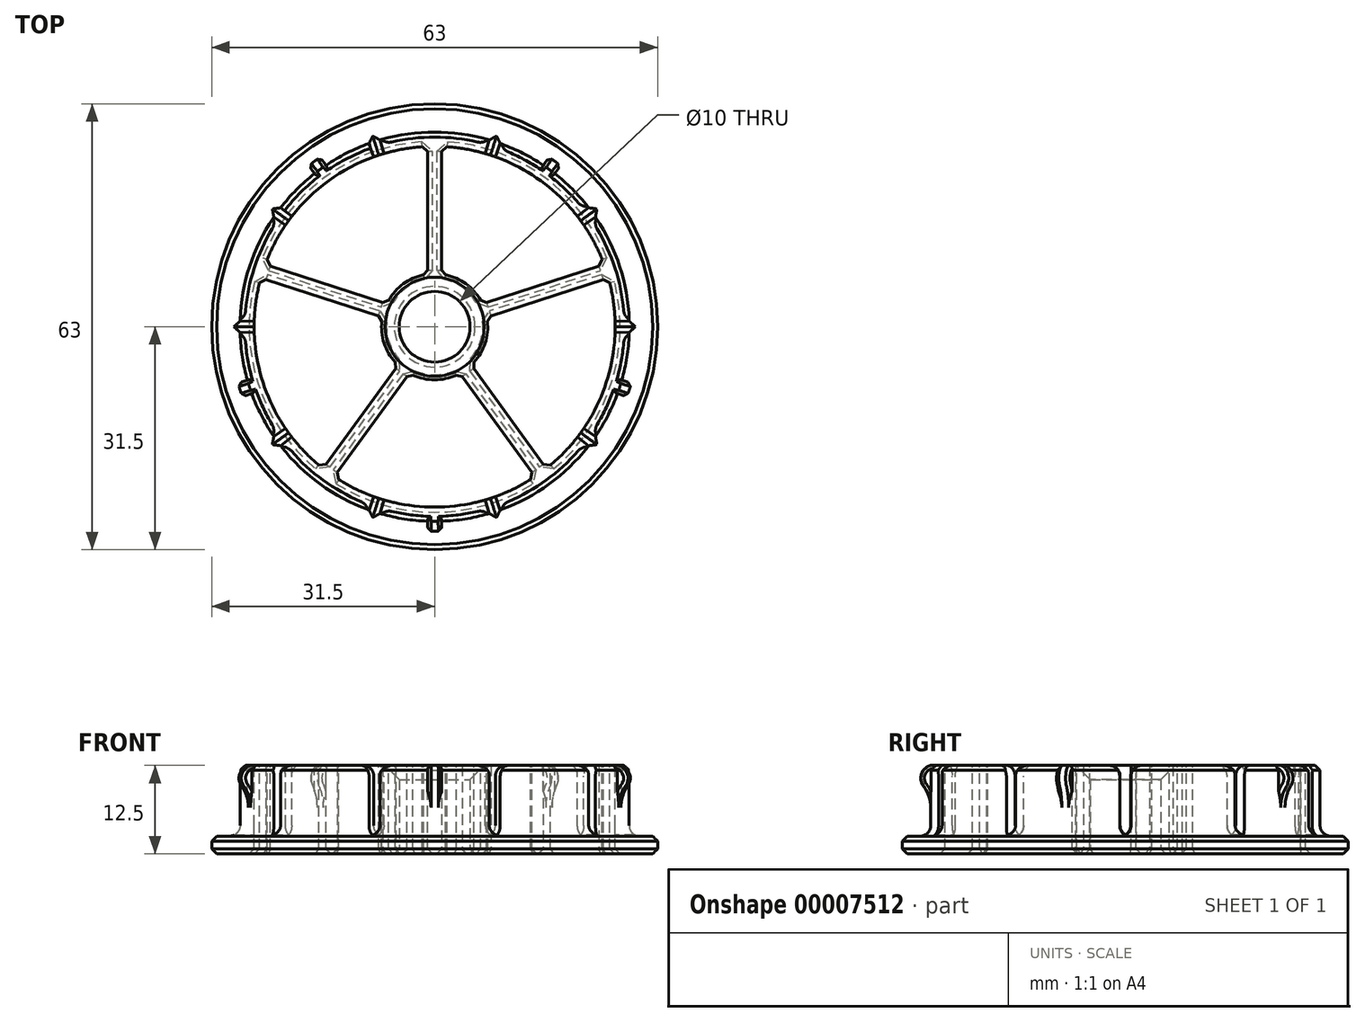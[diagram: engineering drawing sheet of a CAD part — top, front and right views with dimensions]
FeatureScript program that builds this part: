
annotation { "Feature Type Name" : "Feature", "Feature Type Description" : "" }
export const myFeature = defineFeature(function(context is Context, id is Id, definition is map)
    precondition{}
    {
        {
            var Q0;
            Q0=qCreatedBy(makeId("Front.planeOp"),FACE);
            var sketch = newSketch(context, id + "F0", { "sketchPlane" : qUnion([Q0])});
            skLineSegment(sketch, "E0", {"start": v(0, 0) * mm, "end": v(-63, 0) * mm, "construction": true});
            skLineSegment(sketch, "E1", {"start": v(-31.5, 0) * mm, "end": v(-31.5, 2.5) * mm});
            skLineSegment(sketch, "E2", {"start": v(-31.5, 2.5) * mm, "end": v(-27.5, 2.5) * mm});
            skLineSegment(sketch, "E3", {"start": v(-27.5, 2.5) * mm, "end": v(-27.5, 8.9) * mm});
            skLineSegment(sketch, "E4", {"start": v(-31.5, 0) * mm, "end": v(-5, 0) * mm});
            skLineSegment(sketch, "E5", {"start": v(-5, 0) * mm, "end": v(-5, 12.5) * mm});
            skLineSegment(sketch, "E6", {"start": v(-5, 12.5) * mm, "end": v(-27.5, 12.5) * mm});
            skLineSegment(sketch, "E7", {"start": v(0, 0) * mm, "end": v(0, 12.5) * mm, "construction": true});
            skLineSegment(sketch, "E8.0.MirrorCS", {"start": v(5, 0) * mm, "end": v(5, 12.5) * mm});
            skLineSegment(sketch, "E9.0.MirrorCS", {"start": v(5, 12.5) * mm, "end": v(27.5, 12.5) * mm});
            skLineSegment(sketch, "E10.0.MirrorCS", {"start": v(27.5, 2.5) * mm, "end": v(27.5, 12.5) * mm});
            skLineSegment(sketch, "E11.0.MirrorCS", {"start": v(31.5, 0) * mm, "end": v(31.5, 2.5) * mm});
            skLineSegment(sketch, "E12.0.MirrorCS", {"start": v(31.5, 0) * mm, "end": v(5, 0) * mm});
            skLineSegment(sketch, "E13.0.MirrorCS", {"start": v(31.5, 2.5) * mm, "end": v(27.5, 2.5) * mm});
            skArc(sketch, "E14", {"start": v(-27.5, 12.5) * mm, "mid": v(-28.9, 10.7) * mm, "end": v(-27.5, 8.9) * mm});
            skSolve(sketch);
        }
        {
            var Q0;
            Q0=makeQuery(id+"F0.imprint","IMPRINT",FACE,{"disambiguationData":[TD([[makeQuery(id+"F0.imprint","IMPRINT",EDGE,{"derivedFrom":sQuery(id+"F0.wireOp",EDGE,"E1")}),-1.0]])]});
            var Q1;
            Q1=sQuery(id+"F0.wireOp",EDGE,"E7");
            revolve(context, id + "F1", {"entities" : qUnion([Q0]), "axis" : qUnion([Q1]), "revolveType" : RevolveType.FULL});
        }
        {
            var Q0;
            Q0=makeQuery(id+"F1.opRevolve","SWEPT_FACE",FACE,{"disambiguationData":[OSD([sQuery(id+"F0.wireOp",EDGE,"E6")])]});
            var sketch = newSketch(context, id + "F2", { "sketchPlane" : qUnion([Q0])});
            skCircle(sketch, "E15.0", {"center": v(0, 0) * mm, "radius": 31.5 * mm});
            skCircle(sketch, "E15.1", {"center": v(0, 0) * mm, "radius": 5 * mm});
            skCircle(sketch, "E16.0", {"center": v(0, 0) * mm, "radius": 27.5 * mm});
            skCircle(sketch, "E17", {"center": v(0, 0) * mm, "radius": 7.5 * mm});
            skCircle(sketch, "E18", {"center": v(0, 0) * mm, "radius": 25.5 * mm});
            skLineSegment(sketch, "E19", {"start": v(0, 0) * mm, "end": v(0, 31.5) * mm, "construction": true});
            skLineSegment(sketch, "E20", {"start": v(-1, 7.43) * mm, "end": v(-1, 25.48) * mm});
            skLineSegment(sketch, "E21.0.MirrorCS", {"start": v(1, 7.43) * mm, "end": v(1, 25.48) * mm});
            skLineSegment(sketch, "E22.1.0", {"start": v(-7.38, 1.35) * mm, "end": v(-24.54, 6.92) * mm});
            skLineSegment(sketch, "E22.1.1", {"start": v(-6.76, 3.25) * mm, "end": v(-23.92, 8.82) * mm});
            skLineSegment(sketch, "E22.2.0", {"start": v(-3.56, -6.6) * mm, "end": v(-14.17, -21.2) * mm});
            skLineSegment(sketch, "E22.2.1", {"start": v(-5.18, -5.43) * mm, "end": v(-15.79, -20.03) * mm});
            skLineSegment(sketch, "E22.3.0", {"start": v(5.18, -5.43) * mm, "end": v(15.79, -20.03) * mm});
            skLineSegment(sketch, "E22.3.1", {"start": v(3.56, -6.6) * mm, "end": v(14.17, -21.2) * mm});
            skLineSegment(sketch, "E22.4.0", {"start": v(6.76, 3.25) * mm, "end": v(23.92, 8.82) * mm});
            skLineSegment(sketch, "E22.4.1", {"start": v(7.38, 1.35) * mm, "end": v(24.54, 6.92) * mm});
            skLineSegment(sketch, "E23", {"start": v(16.16, 22.25) * mm, "end": v(-16.16, -22.25) * mm, "construction": true});
            skLineSegment(sketch, "E24", {"start": v(15.34, 22.82) * mm, "end": v(17.7, 26.06) * mm});
            skLineSegment(sketch, "E25.0.MirrorCS", {"start": v(16.96, 21.65) * mm, "end": v(19.31, 24.88) * mm});
            skLineSegment(sketch, "E26.1.0", {"start": v(-16.96, 21.65) * mm, "end": v(-19.31, 24.88) * mm});
            skLineSegment(sketch, "E26.1.1", {"start": v(-15.34, 22.82) * mm, "end": v(-17.7, 26.06) * mm});
            skLineSegment(sketch, "E26.2.0", {"start": v(-25.83, -9.44) * mm, "end": v(-29.63, -10.68) * mm});
            skLineSegment(sketch, "E26.2.1", {"start": v(-26.45, -7.54) * mm, "end": v(-30.25, -8.78) * mm});
            skLineSegment(sketch, "E26.3.0", {"start": v(1, -27.48) * mm, "end": v(1, -31.48) * mm});
            skLineSegment(sketch, "E26.3.1", {"start": v(-1, -27.48) * mm, "end": v(-1, -31.48) * mm});
            skLineSegment(sketch, "E26.4.0", {"start": v(26.45, -7.54) * mm, "end": v(30.25, -8.78) * mm});
            skLineSegment(sketch, "E26.4.1", {"start": v(25.83, -9.44) * mm, "end": v(29.63, -10.68) * mm});
            skSolve(sketch);
        }
        {
            var Q0;
            {var subQ10=sQuery(id+"F2.wireOp",EDGE,"E16.0");var subQ16=makeQuery(id+"F2.imprint","INTERSECT",VERTEX,{"derivedFrom":[subQ10,sQuery(id+"F2.wireOp",EDGE,"E26.1.0")]});Q0=makeQuery(id+"F2.imprint","IMPRINT",FACE,{"disambiguationData":[TD([[makeQuery(id+"F2.imprint","IMPRINT",EDGE,{"disambiguationData":[TD([[subQ16,-1.0]])],"derivedFrom":subQ10}),-1.0]])]});}
            var sketch = newSketch(context, id + "F3", { "sketchPlane" : qUnion([Q0])});
            skLineSegment(sketch, "E27.0", {"start": v(0, 0) * mm, "end": v(0, 31.5) * mm, "construction": true});
            skLineSegment(sketch, "E27.1", {"start": v(16.16, 22.25) * mm, "end": v(-16.16, -22.25) * mm, "construction": true});
            skCircle(sketch, "E27.2", {"center": v(0, 0) * mm, "radius": 25.5 * mm});
            skCircle(sketch, "E27.3", {"center": v(0, 0) * mm, "radius": 27.5 * mm});
            skPoint(sketch, "E28", {"position": v(0, 27.5) * mm});
            skLineSegment(sketch, "E29", {"start": v(0, 27.5) * mm, "end": v(8.5, 26.15) * mm, "construction": true});
            skLineSegment(sketch, "E30", {"start": v(8.5, 26.15) * mm, "end": v(16.16, 22.25) * mm, "construction": true});
            skLineSegment(sketch, "E31", {"start": v(0, 0) * mm, "end": v(8.5, 26.15) * mm, "construction": true});
            skLineSegment(sketch, "E32", {"start": v(7.73, 26.4) * mm, "end": v(7.16, 24.47) * mm});
            skLineSegment(sketch, "E33.0.MirrorCS", {"start": v(9.26, 25.9) * mm, "end": v(8.59, 24) * mm});
            skLineSegment(sketch, "E34.1.0", {"start": v(-9.26, 25.9) * mm, "end": v(-8.59, 24) * mm});
            skLineSegment(sketch, "E34.1.1", {"start": v(-7.73, 26.4) * mm, "end": v(-7.16, 24.47) * mm});
            skLineSegment(sketch, "E34.2.0", {"start": v(-22.71, 15.5) * mm, "end": v(-21.06, 14.38) * mm});
            skLineSegment(sketch, "E34.2.1", {"start": v(-21.76, 16.81) * mm, "end": v(-20.18, 15.59) * mm});
            skLineSegment(sketch, "E34.3.0", {"start": v(-27.49, -0.8) * mm, "end": v(-25.49, -0.75) * mm});
            skLineSegment(sketch, "E34.3.1", {"start": v(-27.49, 0.8) * mm, "end": v(-25.49, 0.75) * mm});
            skLineSegment(sketch, "E34.4.0", {"start": v(-21.76, -16.81) * mm, "end": v(-20.18, -15.59) * mm});
            skLineSegment(sketch, "E34.4.1", {"start": v(-22.71, -15.5) * mm, "end": v(-21.06, -14.38) * mm});
            skLineSegment(sketch, "E34.5.0", {"start": v(-7.73, -26.4) * mm, "end": v(-7.16, -24.47) * mm});
            skLineSegment(sketch, "E34.5.1", {"start": v(-9.26, -25.9) * mm, "end": v(-8.59, -24) * mm});
            skLineSegment(sketch, "E34.6.0", {"start": v(9.26, -25.9) * mm, "end": v(8.59, -24) * mm});
            skLineSegment(sketch, "E34.6.1", {"start": v(7.73, -26.4) * mm, "end": v(7.16, -24.47) * mm});
            skLineSegment(sketch, "E34.7.0", {"start": v(22.71, -15.5) * mm, "end": v(21.06, -14.38) * mm});
            skLineSegment(sketch, "E34.7.1", {"start": v(21.76, -16.81) * mm, "end": v(20.18, -15.59) * mm});
            skLineSegment(sketch, "E34.8.0", {"start": v(27.49, 0.8) * mm, "end": v(25.49, 0.75) * mm});
            skLineSegment(sketch, "E34.8.1", {"start": v(27.49, -0.8) * mm, "end": v(25.49, -0.75) * mm});
            skLineSegment(sketch, "E34.9.0", {"start": v(21.76, 16.81) * mm, "end": v(20.18, 15.59) * mm});
            skLineSegment(sketch, "E34.9.1", {"start": v(22.71, 15.5) * mm, "end": v(21.06, 14.38) * mm});
            skSolve(sketch);
        }
        {
            var Q0;
            {var subQ2=sQuery(id+"F2.wireOp",EDGE,"E20");Q0=makeQuery(id+"F2.imprint","IMPRINT",FACE,{"disambiguationData":[TD([[makeQuery(id+"F2.imprint","IMPRINT",EDGE,{"derivedFrom":subQ2}),1.0]])]});}
            var Q1;
            {var subQ1=sQuery(id+"F2.wireOp",EDGE,"E21.0.MirrorCS");Q1=makeQuery(id+"F2.imprint","IMPRINT",FACE,{"disambiguationData":[TD([[makeQuery(id+"F2.imprint","IMPRINT",EDGE,{"derivedFrom":subQ1}),-1.0]])]});}
            var Q2;
            {var subQ1=sQuery(id+"F2.wireOp",EDGE,"E22.3.0");Q2=makeQuery(id+"F2.imprint","IMPRINT",FACE,{"disambiguationData":[TD([[makeQuery(id+"F2.imprint","IMPRINT",EDGE,{"derivedFrom":subQ1}),1.0]])]});}
            var Q3;
            {var subQ2=sQuery(id+"F2.wireOp",EDGE,"E22.2.0");Q3=makeQuery(id+"F2.imprint","IMPRINT",FACE,{"disambiguationData":[TD([[makeQuery(id+"F2.imprint","IMPRINT",EDGE,{"derivedFrom":subQ2}),1.0]])]});}
            var Q4;
            {var subQ1=sQuery(id+"F2.wireOp",EDGE,"E22.1.0");Q4=makeQuery(id+"F2.imprint","IMPRINT",FACE,{"disambiguationData":[TD([[makeQuery(id+"F2.imprint","IMPRINT",EDGE,{"derivedFrom":subQ1}),1.0]])]});}
            var Q5;
            Q5=makeQuery(id+"F1.opRevolve","SWEPT_FACE",FACE,{"disambiguationData":[OSD([sQuery(id+"F0.wireOp",EDGE,"E4")])]});
            extrude(context, id + "F4", {"entities" : qUnion([Q0, Q1, Q2, Q3, Q4]), "operationType" : NewBodyOperationType.REMOVE, "endBound" : BoundingType.UP_TO_SURFACE, "oppositeDirection" : true, "endBoundEntityFace" : qUnion([Q5]), "depth" : 25 * mm});
        }
        {
            var Q0;
            {var subQ0=sQuery(id+"F2.wireOp",EDGE,"E24");Q0=makeQuery(id+"F2.imprint","IMPRINT",FACE,{"disambiguationData":[TD([[makeQuery(id+"F2.imprint","IMPRINT",EDGE,{"derivedFrom":subQ0}),1.0]])]});}
            var Q1;
            {var subQ1=sQuery(id+"F2.wireOp",EDGE,"E25.0.MirrorCS");Q1=makeQuery(id+"F2.imprint","IMPRINT",FACE,{"disambiguationData":[TD([[makeQuery(id+"F2.imprint","IMPRINT",EDGE,{"derivedFrom":subQ1}),-1.0]])]});}
            var Q2;
            {var subQ1=sQuery(id+"F2.wireOp",EDGE,"E26.3.0");Q2=makeQuery(id+"F2.imprint","IMPRINT",FACE,{"disambiguationData":[TD([[makeQuery(id+"F2.imprint","IMPRINT",EDGE,{"derivedFrom":subQ1}),1.0]])]});}
            var Q3;
            {var subQ1=sQuery(id+"F2.wireOp",EDGE,"E26.2.0");Q3=makeQuery(id+"F2.imprint","IMPRINT",FACE,{"disambiguationData":[TD([[makeQuery(id+"F2.imprint","IMPRINT",EDGE,{"derivedFrom":subQ1}),1.0]])]});}
            var Q4;
            {var subQ1=sQuery(id+"F2.wireOp",EDGE,"E26.1.0");Q4=makeQuery(id+"F2.imprint","IMPRINT",FACE,{"disambiguationData":[TD([[makeQuery(id+"F2.imprint","IMPRINT",EDGE,{"derivedFrom":subQ1}),1.0]])]});}
            extrude(context, id + "F5", {"entities" : qUnion([Q0, Q1, Q2, Q3, Q4]), "operationType" : NewBodyOperationType.REMOVE, "endBound" : BoundingType.UP_TO_NEXT, "oppositeDirection" : true, "depth" : 25 * mm});
        }
        {
            var Q0;
            {var subQ1=sQuery(id+"F3.wireOp",EDGE,"E34.1.0");Q0=makeQuery(id+"F3.imprint","IMPRINT",FACE,{"disambiguationData":[TD([[makeQuery(id+"F3.imprint","IMPRINT",EDGE,{"derivedFrom":subQ1}),1.0]])]});}
            var Q1;
            {var subQ1=sQuery(id+"F3.wireOp",EDGE,"E34.2.0");Q1=makeQuery(id+"F3.imprint","IMPRINT",FACE,{"disambiguationData":[TD([[makeQuery(id+"F3.imprint","IMPRINT",EDGE,{"derivedFrom":subQ1}),1.0]])]});}
            var Q2;
            {var subQ1=sQuery(id+"F3.wireOp",EDGE,"E34.3.0");Q2=makeQuery(id+"F3.imprint","IMPRINT",FACE,{"disambiguationData":[TD([[makeQuery(id+"F3.imprint","IMPRINT",EDGE,{"derivedFrom":subQ1}),1.0]])]});}
            var Q3;
            {var subQ1=sQuery(id+"F3.wireOp",EDGE,"E34.4.0");Q3=makeQuery(id+"F3.imprint","IMPRINT",FACE,{"disambiguationData":[TD([[makeQuery(id+"F3.imprint","IMPRINT",EDGE,{"derivedFrom":subQ1}),1.0]])]});}
            var Q4;
            {var subQ1=sQuery(id+"F3.wireOp",EDGE,"E34.5.0");Q4=makeQuery(id+"F3.imprint","IMPRINT",FACE,{"disambiguationData":[TD([[makeQuery(id+"F3.imprint","IMPRINT",EDGE,{"derivedFrom":subQ1}),1.0]])]});}
            var Q5;
            {var subQ1=sQuery(id+"F3.wireOp",EDGE,"E34.6.0");Q5=makeQuery(id+"F3.imprint","IMPRINT",FACE,{"disambiguationData":[TD([[makeQuery(id+"F3.imprint","IMPRINT",EDGE,{"derivedFrom":subQ1}),1.0]])]});}
            var Q6;
            {var subQ1=sQuery(id+"F3.wireOp",EDGE,"E34.7.0");Q6=makeQuery(id+"F3.imprint","IMPRINT",FACE,{"disambiguationData":[TD([[makeQuery(id+"F3.imprint","IMPRINT",EDGE,{"derivedFrom":subQ1}),1.0]])]});}
            var Q7;
            {var subQ1=sQuery(id+"F3.wireOp",EDGE,"E34.8.0");Q7=makeQuery(id+"F3.imprint","IMPRINT",FACE,{"disambiguationData":[TD([[makeQuery(id+"F3.imprint","IMPRINT",EDGE,{"derivedFrom":subQ1}),1.0]])]});}
            var Q8;
            {var subQ1=sQuery(id+"F3.wireOp",EDGE,"E34.9.0");Q8=makeQuery(id+"F3.imprint","IMPRINT",FACE,{"disambiguationData":[TD([[makeQuery(id+"F3.imprint","IMPRINT",EDGE,{"derivedFrom":subQ1}),1.0]])]});}
            var Q9;
            {var subQ1=sQuery(id+"F3.wireOp",EDGE,"E32");Q9=makeQuery(id+"F3.imprint","IMPRINT",FACE,{"disambiguationData":[TD([[makeQuery(id+"F3.imprint","IMPRINT",EDGE,{"derivedFrom":subQ1}),1.0]])]});}
            var Q10;
            Q10=makeQuery(id+"F1.opRevolve","SWEPT_FACE",FACE,{"disambiguationData":[OSD([sQuery(id+"F0.wireOp",EDGE,"E2")])]});
            extrude(context, id + "F6", {"entities" : qUnion([Q0, Q1, Q2, Q3, Q4, Q5, Q6, Q7, Q8, Q9]), "operationType" : NewBodyOperationType.REMOVE, "endBound" : BoundingType.UP_TO_SURFACE, "oppositeDirection" : true, "endBoundEntityFace" : qUnion([Q10]), "depth" : 10 * mm});
        }
        {
            var Q0;
            {var subQ0=sQuery(id+"F0.wireOp",EDGE,"E6");var subQ1=sQuery(id+"F0.wireOp",EDGE,"E14");var subQ2=makeQuery(id+"F1.opRevolve","SWEPT_EDGE",EDGE,{"disambiguationData":[OSD([subQ0,subQ1])]});var subQ3=sQuery(id+"F2.wireOp",EDGE,"E16.0");Q0=makeQuery(id+"F5.boolean.opBoolean","MERGE",EDGE,{"derivedFrom":[subQ2,makeQuery(id+"F5.opExtrude","CAP_EDGE",EDGE,{"disambiguationData":[OSD([subQ0,subQ1,subQ3]),TDD([subQ2,makeQuery(id+"F2.imprint","IMPRINT",EDGE,{"disambiguationData":[TD([[makeQuery(id+"F2.imprint","INTERSECT",VERTEX,{"derivedFrom":[subQ3,sQuery(id+"F2.wireOp",EDGE,"E26.1.0")]}),1.0]])],"derivedFrom":subQ3})])],"isStart":true})]});}
            var Q1;
            {var subQ0=sQuery(id+"F0.wireOp",EDGE,"E6");var subQ1=sQuery(id+"F0.wireOp",EDGE,"E14");var subQ2=makeQuery(id+"F1.opRevolve","SWEPT_EDGE",EDGE,{"disambiguationData":[OSD([subQ0,subQ1])]});var subQ3=sQuery(id+"F2.wireOp",EDGE,"E16.0");Q1=makeQuery(id+"F5.boolean.opBoolean","MERGE",EDGE,{"derivedFrom":[subQ2,makeQuery(id+"F5.opExtrude","CAP_EDGE",EDGE,{"disambiguationData":[OSD([subQ0,subQ1,subQ3]),TDD([subQ2,makeQuery(id+"F2.imprint","IMPRINT",EDGE,{"disambiguationData":[TD([[makeQuery(id+"F2.imprint","INTERSECT",VERTEX,{"derivedFrom":[subQ3,sQuery(id+"F2.wireOp",EDGE,"E26.2.0")]}),1.0]])],"derivedFrom":subQ3})])],"isStart":true})]});}
            var Q2;
            {var subQ0=sQuery(id+"F0.wireOp",EDGE,"E6");var subQ1=sQuery(id+"F0.wireOp",EDGE,"E14");var subQ2=makeQuery(id+"F1.opRevolve","SWEPT_EDGE",EDGE,{"disambiguationData":[OSD([subQ0,subQ1])]});var subQ3=sQuery(id+"F2.wireOp",EDGE,"E16.0");Q2=makeQuery(id+"F5.boolean.opBoolean","MERGE",EDGE,{"derivedFrom":[subQ2,makeQuery(id+"F5.opExtrude","CAP_EDGE",EDGE,{"disambiguationData":[OSD([subQ0,subQ1,subQ3]),TDD([subQ2,makeQuery(id+"F2.imprint","IMPRINT",EDGE,{"disambiguationData":[TD([[makeQuery(id+"F2.imprint","INTERSECT",VERTEX,{"derivedFrom":[subQ3,sQuery(id+"F2.wireOp",EDGE,"E26.3.0")]}),1.0]])],"derivedFrom":subQ3})])],"isStart":true})]});}
            var Q3;
            {var subQ0=sQuery(id+"F0.wireOp",EDGE,"E6");var subQ1=sQuery(id+"F0.wireOp",EDGE,"E14");var subQ2=makeQuery(id+"F1.opRevolve","SWEPT_EDGE",EDGE,{"disambiguationData":[OSD([subQ0,subQ1])]});var subQ3=sQuery(id+"F2.wireOp",EDGE,"E16.0");Q3=makeQuery(id+"F5.boolean.opBoolean","MERGE",EDGE,{"derivedFrom":[subQ2,makeQuery(id+"F5.opExtrude","CAP_EDGE",EDGE,{"disambiguationData":[OSD([subQ0,subQ1,subQ3]),TDD([subQ2,makeQuery(id+"F2.imprint","IMPRINT",EDGE,{"disambiguationData":[TD([[makeQuery(id+"F2.imprint","INTERSECT",VERTEX,{"derivedFrom":[subQ3,sQuery(id+"F2.wireOp",EDGE,"E25.0.MirrorCS")]}),-1.0]])],"derivedFrom":subQ3})])],"isStart":true})]});}
            var Q4;
            {var subQ0=sQuery(id+"F0.wireOp",EDGE,"E6");var subQ1=sQuery(id+"F0.wireOp",EDGE,"E14");var subQ2=makeQuery(id+"F1.opRevolve","SWEPT_EDGE",EDGE,{"disambiguationData":[OSD([subQ0,subQ1])]});var subQ3=sQuery(id+"F2.wireOp",EDGE,"E16.0");Q4=makeQuery(id+"F5.boolean.opBoolean","MERGE",EDGE,{"derivedFrom":[subQ2,makeQuery(id+"F5.opExtrude","CAP_EDGE",EDGE,{"disambiguationData":[OSD([subQ0,subQ1,subQ3]),TDD([subQ2,makeQuery(id+"F2.imprint","IMPRINT",EDGE,{"disambiguationData":[TD([[makeQuery(id+"F2.imprint","INTERSECT",VERTEX,{"derivedFrom":[subQ3,sQuery(id+"F2.wireOp",EDGE,"E24")]}),1.0]])],"derivedFrom":subQ3})])],"isStart":true})]});}
            var Q5;
            {var subQ0=sQuery(id+"F2.wireOp",EDGE,"E18");Q5=makeQuery(id+"F4.boolean.opBoolean","COPY",EDGE,{"derivedFrom":makeQuery(id+"F4.opExtrude","CAP_EDGE",EDGE,{"disambiguationData":[OSD([subQ0]),TDD([makeQuery(id+"F2.imprint","IMPRINT",EDGE,{"disambiguationData":[TD([[makeQuery(id+"F2.imprint","INTERSECT",VERTEX,{"derivedFrom":[subQ0,sQuery(id+"F2.wireOp",EDGE,"E20")]}),-1.0]])],"derivedFrom":subQ0})])],"isStart":true})});}
            var Q6;
            Q6=makeQuery(id+"F4.boolean.opBoolean","COPY",EDGE,{"derivedFrom":makeQuery(id+"F4.opExtrude","CAP_EDGE",EDGE,{"disambiguationData":[OSD([sQuery(id+"F2.wireOp",EDGE,"E22.1.1")])],"isStart":true})});
            var Q7;
            {var subQ0=sQuery(id+"F2.wireOp",EDGE,"E17");Q7=makeQuery(id+"F4.boolean.opBoolean","COPY",EDGE,{"derivedFrom":makeQuery(id+"F4.opExtrude","CAP_EDGE",EDGE,{"disambiguationData":[OSD([subQ0]),TDD([makeQuery(id+"F2.imprint","IMPRINT",EDGE,{"disambiguationData":[TD([[makeQuery(id+"F2.imprint","INTERSECT",VERTEX,{"derivedFrom":[subQ0,sQuery(id+"F2.wireOp",EDGE,"E20")]}),-1.0]])],"derivedFrom":subQ0})])],"isStart":true})});}
            var Q8;
            Q8=makeQuery(id+"F4.boolean.opBoolean","COPY",EDGE,{"derivedFrom":makeQuery(id+"F4.opExtrude","CAP_EDGE",EDGE,{"disambiguationData":[OSD([sQuery(id+"F2.wireOp",EDGE,"E20")])],"isStart":true})});
            var Q9;
            Q9=makeQuery(id+"F4.boolean.opBoolean","COPY",EDGE,{"derivedFrom":makeQuery(id+"F4.opExtrude","CAP_EDGE",EDGE,{"disambiguationData":[OSD([sQuery(id+"F2.wireOp",EDGE,"E22.1.0")])],"isStart":true})});
            var Q10;
            {var subQ0=sQuery(id+"F2.wireOp",EDGE,"E18");Q10=makeQuery(id+"F4.boolean.opBoolean","COPY",EDGE,{"derivedFrom":makeQuery(id+"F4.opExtrude","CAP_EDGE",EDGE,{"disambiguationData":[OSD([subQ0]),TDD([makeQuery(id+"F2.imprint","IMPRINT",EDGE,{"disambiguationData":[TD([[makeQuery(id+"F2.imprint","INTERSECT",VERTEX,{"derivedFrom":[subQ0,sQuery(id+"F2.wireOp",EDGE,"E22.1.0")]}),-1.0]])],"derivedFrom":subQ0})])],"isStart":true})});}
            var Q11;
            Q11=makeQuery(id+"F4.boolean.opBoolean","COPY",EDGE,{"derivedFrom":makeQuery(id+"F4.opExtrude","CAP_EDGE",EDGE,{"disambiguationData":[OSD([sQuery(id+"F2.wireOp",EDGE,"E22.2.1")])],"isStart":true})});
            var Q12;
            {var subQ0=sQuery(id+"F2.wireOp",EDGE,"E17");Q12=makeQuery(id+"F4.boolean.opBoolean","COPY",EDGE,{"derivedFrom":makeQuery(id+"F4.opExtrude","CAP_EDGE",EDGE,{"disambiguationData":[OSD([subQ0]),TDD([makeQuery(id+"F2.imprint","IMPRINT",EDGE,{"disambiguationData":[TD([[makeQuery(id+"F2.imprint","INTERSECT",VERTEX,{"derivedFrom":[subQ0,sQuery(id+"F2.wireOp",EDGE,"E22.1.0")]}),-1.0]])],"derivedFrom":subQ0})])],"isStart":true})});}
            var Q13;
            Q13=makeQuery(id+"F4.boolean.opBoolean","COPY",EDGE,{"derivedFrom":makeQuery(id+"F4.opExtrude","CAP_EDGE",EDGE,{"disambiguationData":[OSD([sQuery(id+"F2.wireOp",EDGE,"E22.2.0")])],"isStart":true})});
            var Q14;
            {var subQ0=sQuery(id+"F2.wireOp",EDGE,"E18");Q14=makeQuery(id+"F4.boolean.opBoolean","COPY",EDGE,{"derivedFrom":makeQuery(id+"F4.opExtrude","CAP_EDGE",EDGE,{"disambiguationData":[OSD([subQ0]),TDD([makeQuery(id+"F2.imprint","IMPRINT",EDGE,{"disambiguationData":[TD([[makeQuery(id+"F2.imprint","INTERSECT",VERTEX,{"derivedFrom":[subQ0,sQuery(id+"F2.wireOp",EDGE,"E22.2.0")]}),-1.0]])],"derivedFrom":subQ0})])],"isStart":true})});}
            var Q15;
            {var subQ0=sQuery(id+"F2.wireOp",EDGE,"E17");Q15=makeQuery(id+"F4.boolean.opBoolean","COPY",EDGE,{"derivedFrom":makeQuery(id+"F4.opExtrude","CAP_EDGE",EDGE,{"disambiguationData":[OSD([subQ0]),TDD([makeQuery(id+"F2.imprint","IMPRINT",EDGE,{"disambiguationData":[TD([[makeQuery(id+"F2.imprint","INTERSECT",VERTEX,{"derivedFrom":[subQ0,sQuery(id+"F2.wireOp",EDGE,"E22.2.0")]}),-1.0]])],"derivedFrom":subQ0})])],"isStart":true})});}
            var Q16;
            Q16=makeQuery(id+"F4.boolean.opBoolean","COPY",EDGE,{"derivedFrom":makeQuery(id+"F4.opExtrude","CAP_EDGE",EDGE,{"disambiguationData":[OSD([sQuery(id+"F2.wireOp",EDGE,"E22.3.1")])],"isStart":true})});
            var Q17;
            Q17=makeQuery(id+"F4.boolean.opBoolean","COPY",EDGE,{"derivedFrom":makeQuery(id+"F4.opExtrude","CAP_EDGE",EDGE,{"disambiguationData":[OSD([sQuery(id+"F2.wireOp",EDGE,"E22.3.0")])],"isStart":true})});
            var Q18;
            {var subQ0=sQuery(id+"F2.wireOp",EDGE,"E17");Q18=makeQuery(id+"F4.boolean.opBoolean","COPY",EDGE,{"derivedFrom":makeQuery(id+"F4.opExtrude","CAP_EDGE",EDGE,{"disambiguationData":[OSD([subQ0]),TDD([makeQuery(id+"F2.imprint","IMPRINT",EDGE,{"disambiguationData":[TD([[makeQuery(id+"F2.imprint","INTERSECT",VERTEX,{"derivedFrom":[subQ0,sQuery(id+"F2.wireOp",EDGE,"E22.3.0")]}),-1.0]])],"derivedFrom":subQ0})])],"isStart":true})});}
            var Q19;
            {var subQ0=sQuery(id+"F2.wireOp",EDGE,"E18");Q19=makeQuery(id+"F4.boolean.opBoolean","COPY",EDGE,{"derivedFrom":makeQuery(id+"F4.opExtrude","CAP_EDGE",EDGE,{"disambiguationData":[OSD([subQ0]),TDD([makeQuery(id+"F2.imprint","IMPRINT",EDGE,{"disambiguationData":[TD([[makeQuery(id+"F2.imprint","INTERSECT",VERTEX,{"derivedFrom":[subQ0,sQuery(id+"F2.wireOp",EDGE,"E22.3.0")]}),-1.0]])],"derivedFrom":subQ0})])],"isStart":true})});}
            var Q20;
            Q20=makeQuery(id+"F4.boolean.opBoolean","COPY",EDGE,{"derivedFrom":makeQuery(id+"F4.opExtrude","CAP_EDGE",EDGE,{"disambiguationData":[OSD([sQuery(id+"F2.wireOp",EDGE,"E22.4.1")])],"isStart":true})});
            var Q21;
            Q21=makeQuery(id+"F4.boolean.opBoolean","COPY",EDGE,{"derivedFrom":makeQuery(id+"F4.opExtrude","CAP_EDGE",EDGE,{"disambiguationData":[OSD([sQuery(id+"F2.wireOp",EDGE,"E22.4.0")])],"isStart":true})});
            var Q22;
            {var subQ0=sQuery(id+"F2.wireOp",EDGE,"E17");Q22=makeQuery(id+"F4.boolean.opBoolean","COPY",EDGE,{"derivedFrom":makeQuery(id+"F4.opExtrude","CAP_EDGE",EDGE,{"disambiguationData":[OSD([subQ0]),TDD([makeQuery(id+"F2.imprint","IMPRINT",EDGE,{"disambiguationData":[TD([[makeQuery(id+"F2.imprint","INTERSECT",VERTEX,{"derivedFrom":[subQ0,sQuery(id+"F2.wireOp",EDGE,"E21.0.MirrorCS")]}),1.0]])],"derivedFrom":subQ0})])],"isStart":true})});}
            var Q23;
            {var subQ0=sQuery(id+"F2.wireOp",EDGE,"E18");Q23=makeQuery(id+"F4.boolean.opBoolean","COPY",EDGE,{"derivedFrom":makeQuery(id+"F4.opExtrude","CAP_EDGE",EDGE,{"disambiguationData":[OSD([subQ0]),TDD([makeQuery(id+"F2.imprint","IMPRINT",EDGE,{"disambiguationData":[TD([[makeQuery(id+"F2.imprint","INTERSECT",VERTEX,{"derivedFrom":[subQ0,sQuery(id+"F2.wireOp",EDGE,"E21.0.MirrorCS")]}),1.0]])],"derivedFrom":subQ0})])],"isStart":true})});}
            var Q24;
            Q24=makeQuery(id+"F4.boolean.opBoolean","COPY",EDGE,{"derivedFrom":makeQuery(id+"F4.opExtrude","CAP_EDGE",EDGE,{"disambiguationData":[OSD([sQuery(id+"F2.wireOp",EDGE,"E21.0.MirrorCS")])],"isStart":true})});
            var Q25;
            Q25=makeQuery(id+"F1.opRevolve","SWEPT_EDGE",EDGE,{"disambiguationData":[OSD([sQuery(id+"F0.wireOp",EDGE,"E1"),sQuery(id+"F0.wireOp",EDGE,"E2")])]});
            var Q26;
            Q26=makeQuery(id+"F1.opRevolve","SWEPT_EDGE",EDGE,{"disambiguationData":[OSD([sQuery(id+"F0.wireOp",EDGE,"E1"),sQuery(id+"F0.wireOp",EDGE,"E4")])]});
            var Q27;
            Q27=makeQuery(id+"F4.boolean.opBoolean","COPY",EDGE,{"derivedFrom":makeQuery(id+"F4.opExtrude","SWEPT_EDGE",EDGE,{"disambiguationData":[OSD([sQuery(id+"F2.wireOp",EDGE,"E18"),sQuery(id+"F2.wireOp",EDGE,"E22.4.0")])]})});
            var Q28;
            Q28=makeQuery(id+"F4.boolean.opBoolean","COPY",EDGE,{"derivedFrom":makeQuery(id+"F4.opExtrude","SWEPT_EDGE",EDGE,{"disambiguationData":[OSD([sQuery(id+"F2.wireOp",EDGE,"E18"),sQuery(id+"F2.wireOp",EDGE,"E22.4.1")])]})});
            var Q29;
            Q29=makeQuery(id+"F4.boolean.opBoolean","COPY",EDGE,{"derivedFrom":makeQuery(id+"F4.opExtrude","SWEPT_EDGE",EDGE,{"disambiguationData":[OSD([sQuery(id+"F2.wireOp",EDGE,"E18"),sQuery(id+"F2.wireOp",EDGE,"E22.3.0")])]})});
            var Q30;
            Q30=makeQuery(id+"F4.boolean.opBoolean","COPY",EDGE,{"derivedFrom":makeQuery(id+"F4.opExtrude","SWEPT_EDGE",EDGE,{"disambiguationData":[OSD([sQuery(id+"F2.wireOp",EDGE,"E18"),sQuery(id+"F2.wireOp",EDGE,"E22.3.1")])]})});
            var Q31;
            Q31=makeQuery(id+"F4.boolean.opBoolean","COPY",EDGE,{"derivedFrom":makeQuery(id+"F4.opExtrude","SWEPT_EDGE",EDGE,{"disambiguationData":[OSD([sQuery(id+"F2.wireOp",EDGE,"E18"),sQuery(id+"F2.wireOp",EDGE,"E22.2.0")])]})});
            var Q32;
            Q32=makeQuery(id+"F4.boolean.opBoolean","COPY",EDGE,{"derivedFrom":makeQuery(id+"F4.opExtrude","SWEPT_EDGE",EDGE,{"disambiguationData":[OSD([sQuery(id+"F2.wireOp",EDGE,"E18"),sQuery(id+"F2.wireOp",EDGE,"E22.2.1")])]})});
            var Q33;
            Q33=makeQuery(id+"F4.boolean.opBoolean","COPY",EDGE,{"derivedFrom":makeQuery(id+"F4.opExtrude","SWEPT_EDGE",EDGE,{"disambiguationData":[OSD([sQuery(id+"F2.wireOp",EDGE,"E17"),sQuery(id+"F2.wireOp",EDGE,"E22.1.0")])]})});
            var Q34;
            Q34=makeQuery(id+"F4.boolean.opBoolean","COPY",EDGE,{"derivedFrom":makeQuery(id+"F4.opExtrude","SWEPT_EDGE",EDGE,{"disambiguationData":[OSD([sQuery(id+"F2.wireOp",EDGE,"E17"),sQuery(id+"F2.wireOp",EDGE,"E22.1.1")])]})});
            var Q35;
            Q35=makeQuery(id+"F4.boolean.opBoolean","COPY",EDGE,{"derivedFrom":makeQuery(id+"F4.opExtrude","SWEPT_EDGE",EDGE,{"disambiguationData":[OSD([sQuery(id+"F2.wireOp",EDGE,"E17"),sQuery(id+"F2.wireOp",EDGE,"E20")])]})});
            var Q36;
            Q36=makeQuery(id+"F4.boolean.opBoolean","COPY",EDGE,{"derivedFrom":makeQuery(id+"F4.opExtrude","SWEPT_EDGE",EDGE,{"disambiguationData":[OSD([sQuery(id+"F2.wireOp",EDGE,"E17"),sQuery(id+"F2.wireOp",EDGE,"E21.0.MirrorCS")])]})});
            var Q37;
            Q37=makeQuery(id+"F4.boolean.opBoolean","COPY",EDGE,{"derivedFrom":makeQuery(id+"F4.opExtrude","SWEPT_EDGE",EDGE,{"disambiguationData":[OSD([sQuery(id+"F2.wireOp",EDGE,"E17"),sQuery(id+"F2.wireOp",EDGE,"E22.4.0")])]})});
            var Q38;
            Q38=makeQuery(id+"F4.boolean.opBoolean","COPY",EDGE,{"derivedFrom":makeQuery(id+"F4.opExtrude","SWEPT_EDGE",EDGE,{"disambiguationData":[OSD([sQuery(id+"F2.wireOp",EDGE,"E17"),sQuery(id+"F2.wireOp",EDGE,"E22.4.1")])]})});
            var Q39;
            Q39=makeQuery(id+"F4.boolean.opBoolean","COPY",EDGE,{"derivedFrom":makeQuery(id+"F4.opExtrude","SWEPT_EDGE",EDGE,{"disambiguationData":[OSD([sQuery(id+"F2.wireOp",EDGE,"E18"),sQuery(id+"F2.wireOp",EDGE,"E21.0.MirrorCS")])]})});
            var Q40;
            Q40=makeQuery(id+"F4.boolean.opBoolean","COPY",EDGE,{"derivedFrom":makeQuery(id+"F4.opExtrude","SWEPT_EDGE",EDGE,{"disambiguationData":[OSD([sQuery(id+"F2.wireOp",EDGE,"E18"),sQuery(id+"F2.wireOp",EDGE,"E20")])]})});
            var Q41;
            Q41=makeQuery(id+"F4.boolean.opBoolean","COPY",EDGE,{"derivedFrom":makeQuery(id+"F4.opExtrude","SWEPT_EDGE",EDGE,{"disambiguationData":[OSD([sQuery(id+"F2.wireOp",EDGE,"E18"),sQuery(id+"F2.wireOp",EDGE,"E22.1.0")])]})});
            var Q42;
            Q42=makeQuery(id+"F4.boolean.opBoolean","COPY",EDGE,{"derivedFrom":makeQuery(id+"F4.opExtrude","SWEPT_EDGE",EDGE,{"disambiguationData":[OSD([sQuery(id+"F2.wireOp",EDGE,"E18"),sQuery(id+"F2.wireOp",EDGE,"E22.1.1")])]})});
            var Q43;
            Q43=makeQuery(id+"F4.boolean.opBoolean","COPY",EDGE,{"derivedFrom":makeQuery(id+"F4.opExtrude","SWEPT_EDGE",EDGE,{"disambiguationData":[OSD([sQuery(id+"F2.wireOp",EDGE,"E17"),sQuery(id+"F2.wireOp",EDGE,"E22.3.1")])]})});
            var Q44;
            Q44=makeQuery(id+"F4.boolean.opBoolean","COPY",EDGE,{"derivedFrom":makeQuery(id+"F4.opExtrude","SWEPT_EDGE",EDGE,{"disambiguationData":[OSD([sQuery(id+"F2.wireOp",EDGE,"E17"),sQuery(id+"F2.wireOp",EDGE,"E22.2.0")])]})});
            var Q45;
            Q45=makeQuery(id+"F4.boolean.opBoolean","COPY",EDGE,{"derivedFrom":makeQuery(id+"F4.opExtrude","SWEPT_EDGE",EDGE,{"disambiguationData":[OSD([sQuery(id+"F2.wireOp",EDGE,"E17"),sQuery(id+"F2.wireOp",EDGE,"E22.2.1")])]})});
            var Q46;
            Q46=makeQuery(id+"F4.boolean.opBoolean","COPY",EDGE,{"derivedFrom":makeQuery(id+"F4.opExtrude","SWEPT_EDGE",EDGE,{"disambiguationData":[OSD([sQuery(id+"F2.wireOp",EDGE,"E17"),sQuery(id+"F2.wireOp",EDGE,"E22.3.0")])]})});
            var Q47;
            Q47=makeQuery(id+"F1.opRevolve","SWEPT_FACE",FACE,{"disambiguationData":[OSD([sQuery(id+"F0.wireOp",EDGE,"E4")])]});
            chamfer(context, id + "F7", {"entities" : qUnion([Q0, Q1, Q2, Q3, Q4, Q5, Q6, Q7, Q8, Q9, Q10, Q11, Q12, Q13, Q14, Q15, Q16, Q17, Q18, Q19, Q20, Q21, Q22, Q23, Q24, Q25, Q26, Q27, Q28, Q29, Q30, Q31, Q32, Q33, Q34, Q35, Q36, Q37, Q38, Q39, Q40, Q41, Q42, Q43, Q44, Q45, Q46, Q47]), "width" : 0.7 * mm, "tangentPropagation" : true});
        }
        {
            var Q0;
            Q0=makeQuery(id+"F1.opRevolve","SWEPT_EDGE",EDGE,{"disambiguationData":[OSD([sQuery(id+"F0.wireOp",EDGE,"E5"),sQuery(id+"F0.wireOp",EDGE,"E6")])]});
            chamfer(context, id + "F8", {"entities" : qUnion([Q0]), "width" : 2 * mm, "tangentPropagation" : true});
        }
        {
            var Q0;
            {var subQ0=sQuery(id+"F0.wireOp",EDGE,"E3");var subQ1=sQuery(id+"F0.wireOp",EDGE,"E14");var subQ3=sQuery(id+"F2.wireOp",EDGE,"E26.4.0");Q0=makeQuery(id+"F5.boolean.opBoolean","SPLIT",EDGE,{"disambiguationData":[TD([makeQuery(id+"F5.opExtrude","SWEPT_FACE",FACE,{"disambiguationData":[OSD([subQ3])]})])],"derivedFrom":makeQuery(id+"F1.opRevolve","SWEPT_EDGE",EDGE,{"disambiguationData":[OSD([subQ0,subQ1])]})});}
            var Q1;
            {var subQ0=sQuery(id+"F0.wireOp",EDGE,"E3");var subQ1=sQuery(id+"F0.wireOp",EDGE,"E14");var subQ3=sQuery(id+"F2.wireOp",EDGE,"E24");Q1=makeQuery(id+"F5.boolean.opBoolean","SPLIT",EDGE,{"disambiguationData":[TD([makeQuery(id+"F5.opExtrude","SWEPT_FACE",FACE,{"disambiguationData":[OSD([subQ3])]})])],"derivedFrom":makeQuery(id+"F1.opRevolve","SWEPT_EDGE",EDGE,{"disambiguationData":[OSD([subQ0,subQ1])]})});}
            var Q2;
            {var subQ0=sQuery(id+"F0.wireOp",EDGE,"E3");var subQ1=sQuery(id+"F0.wireOp",EDGE,"E14");var subQ2=sQuery(id+"F2.wireOp",EDGE,"E26.1.0");Q2=makeQuery(id+"F5.boolean.opBoolean","SPLIT",EDGE,{"disambiguationData":[TD([makeQuery(id+"F5.opExtrude","SWEPT_FACE",FACE,{"disambiguationData":[OSD([subQ2])]})])],"derivedFrom":makeQuery(id+"F1.opRevolve","SWEPT_EDGE",EDGE,{"disambiguationData":[OSD([subQ0,subQ1])]})});}
            var Q3;
            {var subQ0=sQuery(id+"F0.wireOp",EDGE,"E3");var subQ1=sQuery(id+"F0.wireOp",EDGE,"E14");var subQ3=sQuery(id+"F2.wireOp",EDGE,"E26.2.0");Q3=makeQuery(id+"F5.boolean.opBoolean","SPLIT",EDGE,{"disambiguationData":[TD([makeQuery(id+"F5.opExtrude","SWEPT_FACE",FACE,{"disambiguationData":[OSD([subQ3])]})])],"derivedFrom":makeQuery(id+"F1.opRevolve","SWEPT_EDGE",EDGE,{"disambiguationData":[OSD([subQ0,subQ1])]})});}
            var Q4;
            {var subQ0=sQuery(id+"F0.wireOp",EDGE,"E3");var subQ1=sQuery(id+"F0.wireOp",EDGE,"E14");var subQ2=sQuery(id+"F2.wireOp",EDGE,"E26.3.0");Q4=makeQuery(id+"F5.boolean.opBoolean","SPLIT",EDGE,{"disambiguationData":[TD([makeQuery(id+"F5.opExtrude","SWEPT_FACE",FACE,{"disambiguationData":[OSD([subQ2])]})])],"derivedFrom":makeQuery(id+"F1.opRevolve","SWEPT_EDGE",EDGE,{"disambiguationData":[OSD([subQ0,subQ1])]})});}
            fillet(context, id + "F9", {"entities" : qUnion([Q0, Q1, Q2, Q3, Q4]), "radius" : 5 * mm, "tangentPropagation" : true, "allowEdgeOverflow" : false});
        }
        {
            var Q0;
            Q0=makeQuery(id+"F5.boolean.opBoolean","INTERSECT",EDGE,{"derivedFrom":[makeQuery(id+"F1.opRevolve","SWEPT_FACE",FACE,{"disambiguationData":[OSD([sQuery(id+"F0.wireOp",EDGE,"E14")])]}),makeQuery(id+"F5.opExtrude","SWEPT_FACE",FACE,{"disambiguationData":[OSD([sQuery(id+"F2.wireOp",EDGE,"E26.1.0")])]})]});
            var Q1;
            Q1=makeQuery(id+"F5.boolean.opBoolean","INTERSECT",EDGE,{"derivedFrom":[makeQuery(id+"F1.opRevolve","SWEPT_FACE",FACE,{"disambiguationData":[OSD([sQuery(id+"F0.wireOp",EDGE,"E14")])]}),makeQuery(id+"F5.opExtrude","SWEPT_FACE",FACE,{"disambiguationData":[OSD([sQuery(id+"F2.wireOp",EDGE,"E26.1.1")])]})]});
            var Q2;
            Q2=makeQuery(id+"F5.boolean.opBoolean","INTERSECT",EDGE,{"derivedFrom":[makeQuery(id+"F1.opRevolve","SWEPT_FACE",FACE,{"disambiguationData":[OSD([sQuery(id+"F0.wireOp",EDGE,"E14")])]}),makeQuery(id+"F5.opExtrude","SWEPT_FACE",FACE,{"disambiguationData":[OSD([sQuery(id+"F2.wireOp",EDGE,"E24")])]})]});
            var Q3;
            Q3=makeQuery(id+"F5.boolean.opBoolean","INTERSECT",EDGE,{"derivedFrom":[makeQuery(id+"F1.opRevolve","SWEPT_FACE",FACE,{"disambiguationData":[OSD([sQuery(id+"F0.wireOp",EDGE,"E14")])]}),makeQuery(id+"F5.opExtrude","SWEPT_FACE",FACE,{"disambiguationData":[OSD([sQuery(id+"F2.wireOp",EDGE,"E25.0.MirrorCS")])]})]});
            var Q4;
            Q4=makeQuery(id+"F5.boolean.opBoolean","INTERSECT",EDGE,{"derivedFrom":[makeQuery(id+"F1.opRevolve","SWEPT_FACE",FACE,{"disambiguationData":[OSD([sQuery(id+"F0.wireOp",EDGE,"E14")])]}),makeQuery(id+"F5.opExtrude","SWEPT_FACE",FACE,{"disambiguationData":[OSD([sQuery(id+"F2.wireOp",EDGE,"E26.4.0")])]})]});
            var Q5;
            Q5=makeQuery(id+"F5.boolean.opBoolean","INTERSECT",EDGE,{"derivedFrom":[makeQuery(id+"F1.opRevolve","SWEPT_FACE",FACE,{"disambiguationData":[OSD([sQuery(id+"F0.wireOp",EDGE,"E14")])]}),makeQuery(id+"F5.opExtrude","SWEPT_FACE",FACE,{"disambiguationData":[OSD([sQuery(id+"F2.wireOp",EDGE,"E26.4.1")])]})]});
            var Q6;
            Q6=makeQuery(id+"F5.boolean.opBoolean","INTERSECT",EDGE,{"derivedFrom":[makeQuery(id+"F1.opRevolve","SWEPT_FACE",FACE,{"disambiguationData":[OSD([sQuery(id+"F0.wireOp",EDGE,"E14")])]}),makeQuery(id+"F5.opExtrude","SWEPT_FACE",FACE,{"disambiguationData":[OSD([sQuery(id+"F2.wireOp",EDGE,"E26.3.0")])]})]});
            var Q7;
            Q7=makeQuery(id+"F5.boolean.opBoolean","INTERSECT",EDGE,{"derivedFrom":[makeQuery(id+"F1.opRevolve","SWEPT_FACE",FACE,{"disambiguationData":[OSD([sQuery(id+"F0.wireOp",EDGE,"E14")])]}),makeQuery(id+"F5.opExtrude","SWEPT_FACE",FACE,{"disambiguationData":[OSD([sQuery(id+"F2.wireOp",EDGE,"E26.3.1")])]})]});
            var Q8;
            Q8=makeQuery(id+"F5.boolean.opBoolean","INTERSECT",EDGE,{"derivedFrom":[makeQuery(id+"F1.opRevolve","SWEPT_FACE",FACE,{"disambiguationData":[OSD([sQuery(id+"F0.wireOp",EDGE,"E14")])]}),makeQuery(id+"F5.opExtrude","SWEPT_FACE",FACE,{"disambiguationData":[OSD([sQuery(id+"F2.wireOp",EDGE,"E26.2.0")])]})]});
            var Q9;
            Q9=makeQuery(id+"F5.boolean.opBoolean","INTERSECT",EDGE,{"derivedFrom":[makeQuery(id+"F1.opRevolve","SWEPT_FACE",FACE,{"disambiguationData":[OSD([sQuery(id+"F0.wireOp",EDGE,"E14")])]}),makeQuery(id+"F5.opExtrude","SWEPT_FACE",FACE,{"disambiguationData":[OSD([sQuery(id+"F2.wireOp",EDGE,"E26.2.1")])]})]});
            chamfer(context, id + "F10", {"entities" : qUnion([Q0, Q1, Q2, Q3, Q4, Q5, Q6, Q7, Q8, Q9]), "width" : 0.5 * mm, "tangentPropagation" : true});
        }
        {
            var Q0;
            Q0=makeQuery(id+"F6.boolean.opBoolean","COPY",EDGE,{"derivedFrom":makeQuery(id+"F6.opExtrude","CAP_EDGE",EDGE,{"disambiguationData":[OSD([sQuery(id+"F3.wireOp",EDGE,"E34.1.1")])],"isStart":false})});
            var Q1;
            Q1=makeQuery(id+"F6.boolean.opBoolean","COPY",EDGE,{"derivedFrom":makeQuery(id+"F6.opExtrude","CAP_EDGE",EDGE,{"disambiguationData":[OSD([sQuery(id+"F3.wireOp",EDGE,"E34.1.0")])],"isStart":false})});
            var Q2;
            Q2=makeQuery(id+"F6.boolean.opBoolean","COPY",EDGE,{"derivedFrom":makeQuery(id+"F6.opExtrude","CAP_EDGE",EDGE,{"disambiguationData":[OSD([sQuery(id+"F3.wireOp",EDGE,"E34.2.1")])],"isStart":false})});
            var Q3;
            Q3=makeQuery(id+"F6.boolean.opBoolean","COPY",EDGE,{"derivedFrom":makeQuery(id+"F6.opExtrude","CAP_EDGE",EDGE,{"disambiguationData":[OSD([sQuery(id+"F3.wireOp",EDGE,"E34.2.0")])],"isStart":false})});
            var Q4;
            Q4=makeQuery(id+"F6.boolean.opBoolean","COPY",EDGE,{"derivedFrom":makeQuery(id+"F6.opExtrude","CAP_EDGE",EDGE,{"disambiguationData":[OSD([sQuery(id+"F3.wireOp",EDGE,"E34.3.1")])],"isStart":false})});
            var Q5;
            {var subQ0=sQuery(id+"F0.wireOp",EDGE,"E2");var subQ1=sQuery(id+"F0.wireOp",EDGE,"E3");var subQ3=sQuery(id+"F3.wireOp",EDGE,"E34.2.0");Q5=makeQuery(id+"F6.boolean.opBoolean","SPLIT",EDGE,{"disambiguationData":[TD([makeQuery(id+"F6.opExtrude","SWEPT_FACE",FACE,{"disambiguationData":[OSD([subQ3])]})])],"derivedFrom":makeQuery(id+"F1.opRevolve","SWEPT_EDGE",EDGE,{"disambiguationData":[OSD([subQ0,subQ1])]})});}
            var Q6;
            {var subQ0=sQuery(id+"F0.wireOp",EDGE,"E2");var subQ1=sQuery(id+"F0.wireOp",EDGE,"E3");var subQ3=sQuery(id+"F3.wireOp",EDGE,"E34.1.0");Q6=makeQuery(id+"F6.boolean.opBoolean","SPLIT",EDGE,{"disambiguationData":[TD([makeQuery(id+"F6.opExtrude","SWEPT_FACE",FACE,{"disambiguationData":[OSD([subQ3])]})])],"derivedFrom":makeQuery(id+"F1.opRevolve","SWEPT_EDGE",EDGE,{"disambiguationData":[OSD([subQ0,subQ1])]})});}
            var Q7;
            Q7=makeQuery(id+"F6.boolean.opBoolean","COPY",EDGE,{"derivedFrom":makeQuery(id+"F6.opExtrude","CAP_EDGE",EDGE,{"disambiguationData":[OSD([sQuery(id+"F3.wireOp",EDGE,"E34.3.0")])],"isStart":false})});
            var Q8;
            {var subQ0=sQuery(id+"F0.wireOp",EDGE,"E2");var subQ1=sQuery(id+"F0.wireOp",EDGE,"E3");var subQ6=sQuery(id+"F3.wireOp",EDGE,"E34.3.0");Q8=makeQuery(id+"F6.boolean.opBoolean","SPLIT",EDGE,{"disambiguationData":[TD([makeQuery(id+"F6.opExtrude","SWEPT_FACE",FACE,{"disambiguationData":[OSD([subQ6])]})])],"derivedFrom":makeQuery(id+"F1.opRevolve","SWEPT_EDGE",EDGE,{"disambiguationData":[OSD([subQ0,subQ1])]})});}
            var Q9;
            Q9=makeQuery(id+"F6.boolean.opBoolean","COPY",EDGE,{"derivedFrom":makeQuery(id+"F6.opExtrude","CAP_EDGE",EDGE,{"disambiguationData":[OSD([sQuery(id+"F3.wireOp",EDGE,"E34.4.1")])],"isStart":false})});
            var Q10;
            Q10=makeQuery(id+"F6.boolean.opBoolean","COPY",EDGE,{"derivedFrom":makeQuery(id+"F6.opExtrude","CAP_EDGE",EDGE,{"disambiguationData":[OSD([sQuery(id+"F3.wireOp",EDGE,"E34.4.0")])],"isStart":false})});
            var Q11;
            {var subQ0=sQuery(id+"F0.wireOp",EDGE,"E2");var subQ1=sQuery(id+"F0.wireOp",EDGE,"E3");var subQ3=sQuery(id+"F3.wireOp",EDGE,"E34.4.0");Q11=makeQuery(id+"F6.boolean.opBoolean","SPLIT",EDGE,{"disambiguationData":[TD([makeQuery(id+"F6.opExtrude","SWEPT_FACE",FACE,{"disambiguationData":[OSD([subQ3])]})])],"derivedFrom":makeQuery(id+"F1.opRevolve","SWEPT_EDGE",EDGE,{"disambiguationData":[OSD([subQ0,subQ1])]})});}
            var Q12;
            Q12=makeQuery(id+"F6.boolean.opBoolean","COPY",EDGE,{"derivedFrom":makeQuery(id+"F6.opExtrude","CAP_EDGE",EDGE,{"disambiguationData":[OSD([sQuery(id+"F3.wireOp",EDGE,"E34.5.1")])],"isStart":false})});
            var Q13;
            Q13=makeQuery(id+"F6.boolean.opBoolean","COPY",EDGE,{"derivedFrom":makeQuery(id+"F6.opExtrude","CAP_EDGE",EDGE,{"disambiguationData":[OSD([sQuery(id+"F3.wireOp",EDGE,"E34.5.0")])],"isStart":false})});
            var Q14;
            {var subQ0=sQuery(id+"F0.wireOp",EDGE,"E2");var subQ1=sQuery(id+"F0.wireOp",EDGE,"E3");var subQ2=sQuery(id+"F3.wireOp",EDGE,"E34.5.0");Q14=makeQuery(id+"F6.boolean.opBoolean","SPLIT",EDGE,{"disambiguationData":[TD([makeQuery(id+"F6.opExtrude","SWEPT_FACE",FACE,{"disambiguationData":[OSD([subQ2])]})])],"derivedFrom":makeQuery(id+"F1.opRevolve","SWEPT_EDGE",EDGE,{"disambiguationData":[OSD([subQ0,subQ1])]})});}
            var Q15;
            Q15=makeQuery(id+"F6.boolean.opBoolean","COPY",EDGE,{"derivedFrom":makeQuery(id+"F6.opExtrude","CAP_EDGE",EDGE,{"disambiguationData":[OSD([sQuery(id+"F3.wireOp",EDGE,"E34.6.1")])],"isStart":false})});
            var Q16;
            Q16=makeQuery(id+"F6.boolean.opBoolean","COPY",EDGE,{"derivedFrom":makeQuery(id+"F6.opExtrude","CAP_EDGE",EDGE,{"disambiguationData":[OSD([sQuery(id+"F3.wireOp",EDGE,"E34.6.0")])],"isStart":false})});
            var Q17;
            {var subQ0=sQuery(id+"F0.wireOp",EDGE,"E2");var subQ1=sQuery(id+"F0.wireOp",EDGE,"E3");var subQ6=sQuery(id+"F3.wireOp",EDGE,"E34.6.0");Q17=makeQuery(id+"F6.boolean.opBoolean","SPLIT",EDGE,{"disambiguationData":[TD([makeQuery(id+"F6.opExtrude","SWEPT_FACE",FACE,{"disambiguationData":[OSD([subQ6])]})])],"derivedFrom":makeQuery(id+"F1.opRevolve","SWEPT_EDGE",EDGE,{"disambiguationData":[OSD([subQ0,subQ1])]})});}
            var Q18;
            Q18=makeQuery(id+"F6.boolean.opBoolean","COPY",EDGE,{"derivedFrom":makeQuery(id+"F6.opExtrude","CAP_EDGE",EDGE,{"disambiguationData":[OSD([sQuery(id+"F3.wireOp",EDGE,"E34.7.1")])],"isStart":false})});
            var Q19;
            Q19=makeQuery(id+"F6.boolean.opBoolean","COPY",EDGE,{"derivedFrom":makeQuery(id+"F6.opExtrude","CAP_EDGE",EDGE,{"disambiguationData":[OSD([sQuery(id+"F3.wireOp",EDGE,"E34.7.0")])],"isStart":false})});
            var Q20;
            {var subQ0=sQuery(id+"F0.wireOp",EDGE,"E2");var subQ1=sQuery(id+"F0.wireOp",EDGE,"E3");var subQ3=sQuery(id+"F3.wireOp",EDGE,"E34.7.0");Q20=makeQuery(id+"F6.boolean.opBoolean","SPLIT",EDGE,{"disambiguationData":[TD([makeQuery(id+"F6.opExtrude","SWEPT_FACE",FACE,{"disambiguationData":[OSD([subQ3])]})])],"derivedFrom":makeQuery(id+"F1.opRevolve","SWEPT_EDGE",EDGE,{"disambiguationData":[OSD([subQ0,subQ1])]})});}
            var Q21;
            Q21=makeQuery(id+"F6.boolean.opBoolean","COPY",EDGE,{"derivedFrom":makeQuery(id+"F6.opExtrude","CAP_EDGE",EDGE,{"disambiguationData":[OSD([sQuery(id+"F3.wireOp",EDGE,"E34.8.1")])],"isStart":false})});
            var Q22;
            Q22=makeQuery(id+"F6.boolean.opBoolean","COPY",EDGE,{"derivedFrom":makeQuery(id+"F6.opExtrude","CAP_EDGE",EDGE,{"disambiguationData":[OSD([sQuery(id+"F3.wireOp",EDGE,"E34.8.0")])],"isStart":false})});
            var Q23;
            {var subQ0=sQuery(id+"F0.wireOp",EDGE,"E2");var subQ1=sQuery(id+"F0.wireOp",EDGE,"E3");var subQ3=sQuery(id+"F3.wireOp",EDGE,"E34.8.0");Q23=makeQuery(id+"F6.boolean.opBoolean","SPLIT",EDGE,{"disambiguationData":[TD([makeQuery(id+"F6.opExtrude","SWEPT_FACE",FACE,{"disambiguationData":[OSD([subQ3])]})])],"derivedFrom":makeQuery(id+"F1.opRevolve","SWEPT_EDGE",EDGE,{"disambiguationData":[OSD([subQ0,subQ1])]})});}
            var Q24;
            Q24=makeQuery(id+"F6.boolean.opBoolean","COPY",EDGE,{"derivedFrom":makeQuery(id+"F6.opExtrude","CAP_EDGE",EDGE,{"disambiguationData":[OSD([sQuery(id+"F3.wireOp",EDGE,"E34.9.1")])],"isStart":false})});
            var Q25;
            {var subQ0=sQuery(id+"F0.wireOp",EDGE,"E2");var subQ1=sQuery(id+"F0.wireOp",EDGE,"E3");var subQ4=sQuery(id+"F3.wireOp",EDGE,"E33.0.MirrorCS");Q25=makeQuery(id+"F6.boolean.opBoolean","SPLIT",EDGE,{"disambiguationData":[TD([makeQuery(id+"F6.opExtrude","SWEPT_FACE",FACE,{"disambiguationData":[OSD([subQ4])]})])],"derivedFrom":makeQuery(id+"F1.opRevolve","SWEPT_EDGE",EDGE,{"disambiguationData":[OSD([subQ0,subQ1])]})});}
            var Q26;
            Q26=makeQuery(id+"F6.boolean.opBoolean","COPY",EDGE,{"derivedFrom":makeQuery(id+"F6.opExtrude","CAP_EDGE",EDGE,{"disambiguationData":[OSD([sQuery(id+"F3.wireOp",EDGE,"E33.0.MirrorCS")])],"isStart":false})});
            var Q27;
            Q27=makeQuery(id+"F6.boolean.opBoolean","COPY",EDGE,{"derivedFrom":makeQuery(id+"F6.opExtrude","CAP_EDGE",EDGE,{"disambiguationData":[OSD([sQuery(id+"F3.wireOp",EDGE,"E34.9.0")])],"isStart":false})});
            var Q28;
            Q28=makeQuery(id+"F6.boolean.opBoolean","COPY",EDGE,{"derivedFrom":makeQuery(id+"F6.opExtrude","CAP_EDGE",EDGE,{"disambiguationData":[OSD([sQuery(id+"F3.wireOp",EDGE,"E32")])],"isStart":false})});
            var Q29;
            {var subQ0=sQuery(id+"F0.wireOp",EDGE,"E2");var subQ1=sQuery(id+"F0.wireOp",EDGE,"E3");var subQ5=sQuery(id+"F3.wireOp",EDGE,"E32");Q29=makeQuery(id+"F6.boolean.opBoolean","SPLIT",EDGE,{"disambiguationData":[TD([makeQuery(id+"F6.opExtrude","SWEPT_FACE",FACE,{"disambiguationData":[OSD([subQ5])]})])],"derivedFrom":makeQuery(id+"F1.opRevolve","SWEPT_EDGE",EDGE,{"disambiguationData":[OSD([subQ0,subQ1])]})});}
            var Q30;
            Q30=makeQuery(id+"F6.boolean.opBoolean","COPY",EDGE,{"derivedFrom":makeQuery(id+"F6.opExtrude","CAP_EDGE",EDGE,{"disambiguationData":[OSD([sQuery(id+"F3.wireOp",EDGE,"E34.3.0")])],"isStart":true})});
            var Q31;
            Q31=makeQuery(id+"F6.boolean.opBoolean","COPY",EDGE,{"derivedFrom":makeQuery(id+"F6.opExtrude","CAP_EDGE",EDGE,{"disambiguationData":[OSD([sQuery(id+"F3.wireOp",EDGE,"E34.4.1")])],"isStart":true})});
            var Q32;
            Q32=makeQuery(id+"F6.boolean.opBoolean","COPY",EDGE,{"derivedFrom":makeQuery(id+"F6.opExtrude","CAP_EDGE",EDGE,{"disambiguationData":[OSD([sQuery(id+"F3.wireOp",EDGE,"E34.3.1")])],"isStart":true})});
            var Q33;
            Q33=makeQuery(id+"F6.boolean.opBoolean","COPY",EDGE,{"derivedFrom":makeQuery(id+"F6.opExtrude","CAP_EDGE",EDGE,{"disambiguationData":[OSD([sQuery(id+"F3.wireOp",EDGE,"E34.2.0")])],"isStart":true})});
            var Q34;
            Q34=makeQuery(id+"F6.boolean.opBoolean","COPY",EDGE,{"derivedFrom":makeQuery(id+"F6.opExtrude","CAP_EDGE",EDGE,{"disambiguationData":[OSD([sQuery(id+"F3.wireOp",EDGE,"E34.2.1")])],"isStart":true})});
            var Q35;
            Q35=makeQuery(id+"F6.boolean.opBoolean","COPY",EDGE,{"derivedFrom":makeQuery(id+"F6.opExtrude","CAP_EDGE",EDGE,{"disambiguationData":[OSD([sQuery(id+"F3.wireOp",EDGE,"E34.1.0")])],"isStart":true})});
            var Q36;
            Q36=makeQuery(id+"F6.boolean.opBoolean","COPY",EDGE,{"derivedFrom":makeQuery(id+"F6.opExtrude","CAP_EDGE",EDGE,{"disambiguationData":[OSD([sQuery(id+"F3.wireOp",EDGE,"E34.1.1")])],"isStart":true})});
            var Q37;
            Q37=makeQuery(id+"F6.boolean.opBoolean","COPY",EDGE,{"derivedFrom":makeQuery(id+"F6.opExtrude","CAP_EDGE",EDGE,{"disambiguationData":[OSD([sQuery(id+"F3.wireOp",EDGE,"E32")])],"isStart":true})});
            var Q38;
            Q38=makeQuery(id+"F6.boolean.opBoolean","COPY",EDGE,{"derivedFrom":makeQuery(id+"F6.opExtrude","CAP_EDGE",EDGE,{"disambiguationData":[OSD([sQuery(id+"F3.wireOp",EDGE,"E33.0.MirrorCS")])],"isStart":true})});
            var Q39;
            Q39=makeQuery(id+"F6.boolean.opBoolean","COPY",EDGE,{"derivedFrom":makeQuery(id+"F6.opExtrude","CAP_EDGE",EDGE,{"disambiguationData":[OSD([sQuery(id+"F3.wireOp",EDGE,"E34.9.0")])],"isStart":true})});
            var Q40;
            Q40=makeQuery(id+"F6.boolean.opBoolean","COPY",EDGE,{"derivedFrom":makeQuery(id+"F6.opExtrude","CAP_EDGE",EDGE,{"disambiguationData":[OSD([sQuery(id+"F3.wireOp",EDGE,"E34.9.1")])],"isStart":true})});
            var Q41;
            Q41=makeQuery(id+"F6.boolean.opBoolean","COPY",EDGE,{"derivedFrom":makeQuery(id+"F6.opExtrude","CAP_EDGE",EDGE,{"disambiguationData":[OSD([sQuery(id+"F3.wireOp",EDGE,"E34.8.0")])],"isStart":true})});
            var Q42;
            Q42=makeQuery(id+"F6.boolean.opBoolean","COPY",EDGE,{"derivedFrom":makeQuery(id+"F6.opExtrude","CAP_EDGE",EDGE,{"disambiguationData":[OSD([sQuery(id+"F3.wireOp",EDGE,"E34.8.1")])],"isStart":true})});
            var Q43;
            Q43=makeQuery(id+"F6.boolean.opBoolean","COPY",EDGE,{"derivedFrom":makeQuery(id+"F6.opExtrude","CAP_EDGE",EDGE,{"disambiguationData":[OSD([sQuery(id+"F3.wireOp",EDGE,"E34.7.0")])],"isStart":true})});
            var Q44;
            Q44=makeQuery(id+"F6.boolean.opBoolean","COPY",EDGE,{"derivedFrom":makeQuery(id+"F6.opExtrude","CAP_EDGE",EDGE,{"disambiguationData":[OSD([sQuery(id+"F3.wireOp",EDGE,"E34.7.1")])],"isStart":true})});
            var Q45;
            Q45=makeQuery(id+"F6.boolean.opBoolean","COPY",EDGE,{"derivedFrom":makeQuery(id+"F6.opExtrude","CAP_EDGE",EDGE,{"disambiguationData":[OSD([sQuery(id+"F3.wireOp",EDGE,"E34.6.0")])],"isStart":true})});
            var Q46;
            Q46=makeQuery(id+"F6.boolean.opBoolean","COPY",EDGE,{"derivedFrom":makeQuery(id+"F6.opExtrude","CAP_EDGE",EDGE,{"disambiguationData":[OSD([sQuery(id+"F3.wireOp",EDGE,"E34.6.1")])],"isStart":true})});
            var Q47;
            Q47=makeQuery(id+"F6.boolean.opBoolean","COPY",EDGE,{"derivedFrom":makeQuery(id+"F6.opExtrude","CAP_EDGE",EDGE,{"disambiguationData":[OSD([sQuery(id+"F3.wireOp",EDGE,"E34.5.0")])],"isStart":true})});
            var Q48;
            Q48=makeQuery(id+"F6.boolean.opBoolean","COPY",EDGE,{"derivedFrom":makeQuery(id+"F6.opExtrude","CAP_EDGE",EDGE,{"disambiguationData":[OSD([sQuery(id+"F3.wireOp",EDGE,"E34.5.1")])],"isStart":true})});
            var Q49;
            Q49=makeQuery(id+"F6.boolean.opBoolean","COPY",EDGE,{"derivedFrom":makeQuery(id+"F6.opExtrude","CAP_EDGE",EDGE,{"disambiguationData":[OSD([sQuery(id+"F3.wireOp",EDGE,"E34.4.0")])],"isStart":true})});
            fillet(context, id + "F11", {"entities" : qUnion([Q0, Q1, Q2, Q3, Q4, Q5, Q6, Q7, Q8, Q9, Q10, Q11, Q12, Q13, Q14, Q15, Q16, Q17, Q18, Q19, Q20, Q21, Q22, Q23, Q24, Q25, Q26, Q27, Q28, Q29, Q30, Q31, Q32, Q33, Q34, Q35, Q36, Q37, Q38, Q39, Q40, Q41, Q42, Q43, Q44, Q45, Q46, Q47, Q48, Q49]), "radius" : 1.5 * mm, "tangentPropagation" : true, "allowEdgeOverflow" : false});
        }
    });
